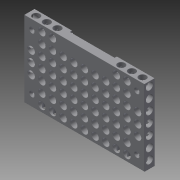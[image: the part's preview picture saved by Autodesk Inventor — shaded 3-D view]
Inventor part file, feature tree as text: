
AUTODESK INVENTOR PART (.ipt)
format: ipt  version: 2013 (Build 170138000, 138)  size: 778,752 bytes
history: native  units: in
note: dims shown in document units (in); Inventor stores cm internally (conversion verified against a paired STEP export)
features: extrude x7, sketch x7, plane x2, mirror x2, fillet x2, chamfer x1, reference x1, projected_geometry x1
ambient origin geometry x8: Origin, YZ Plane, XZ Plane, XY Plane, X Axis, Y Axis, Z Axis, Center Point
bodies: Solid1 (feature_tree)
feature tree (23):
  extrude  "Extrusion1"  Depth=1.5787in
  extrude  "Extrusion4"  Depth=2.6772in
  extrude  "Extrusion5"  Depth=0.1024in
  chamfer  "Chamfer3"  Distance=0.2008in
  extrude  "Extrusion6"  Depth=0.1024in
  extrude  "Extrusion7"  Depth=0.1024in
  extrude  "Extrusion8"  Depth=2.4795in
  plane  "Work Plane2"
  mirror  "Mirror2"
  extrude  "Extrusion9"  Depth=0.0394in TaperAngle=0.0deg
  plane  "Work Plane3"
  mirror  "Mirror3"
  fillet  "Fillet1"  Radius=0.1102in
  fillet  "Fillet2"  Radius=0.1102in
  sketch  "Sketch1"  dims[d0=0.3937in d1=0.0in d37=1.5787in]
  sketch  "Sketch4"  dims[d38=4.2362in d39=2.6772in]
  sketch  "Sketch5"  dims[d42=0.1024in d43=0.1024in]
  reference  "Reference29"
  sketch  "Sketch6"  dims[d44=0.1024in]
  sketch  "Sketch7"  dims[d45=0.1024in]
  sketch  "Sketch8"  dims[d46=0.1024in]
  projected_geometry  "Projected Loop2"
  sketch  "Sketch9"  dims[d48=0.1024in d49=0.2008in d50=0.1024in d51=0.1024in d52=2.4795in d53=0.0394in d54=0.0in d55=0.1102in d56=0.1102in d57=0.1102in d58=0.1102in d59=0.1575in d60=0.0in d61=0.0394in d62=0.0787in d63=45.0deg d64=0.2402in d65=0.0787in d66=0.0787in d67=1.6142in d68=0.0in d69=0.25in d70=0.2136in d71=0.2431in d72=4.3307in d74=0.375in d75=2.7559in d77=0.375in d80=0.2136in d81=0.2431in d82=0.2756in d83=0.0in d84=0.25in d85=0.6181in d86=0.4931in d87=0.25in d88=0.375in d89=0.25in d90=0.375in d91=0.2756in d92=0.0in d93=-1.3386in d94=0.25in d96=0.1772in d97=0.1575in d98=2.7559in d100=0.375in d101=0.3937in d103=0.3937in d105=0.2697in d106=0.2756in d107=0.0in d108=-2.1181in d109=0.0079in d110=0.0079in]
